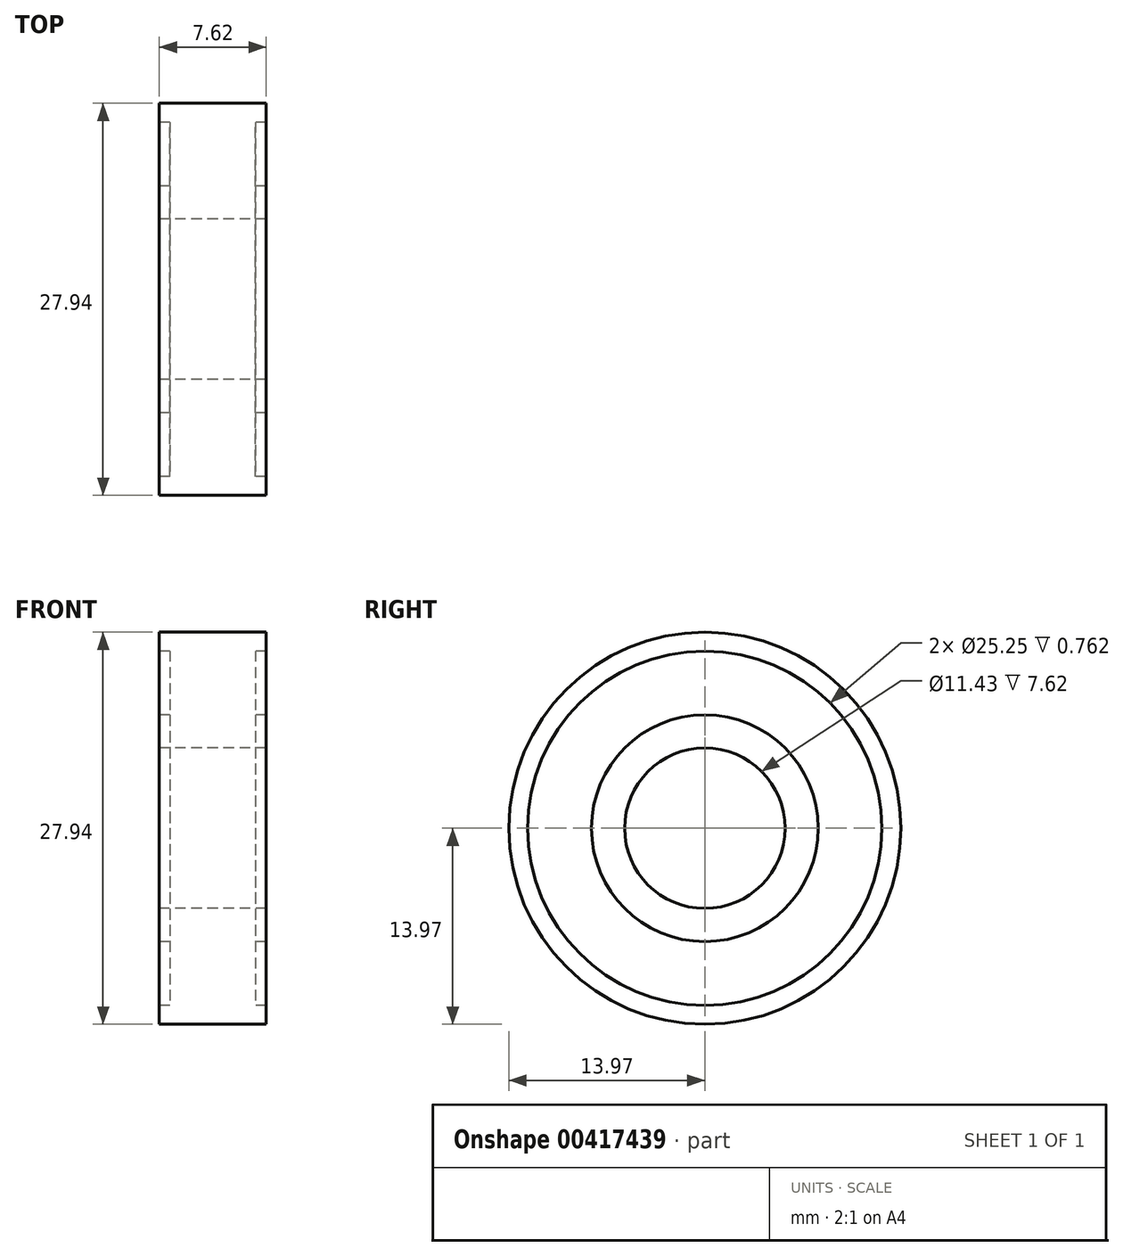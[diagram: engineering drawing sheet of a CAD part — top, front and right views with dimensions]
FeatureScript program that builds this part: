
annotation { "Feature Type Name" : "Feature", "Feature Type Description" : "" }
export const myFeature = defineFeature(function(context is Context, id is Id, definition is map)
    precondition{}
    {
        {
            var Q0;
            Q0=qCreatedBy(makeId("Top.planeOp"),FACE);
            var sketch = newSketch(context, id + "F0", { "sketchPlane" : qUnion([Q0])});
            skLineSegment(sketch, "E0", {"start": v(-3.8, -5.72) * mm, "end": v(3.81, -5.71) * mm});
            skLineSegment(sketch, "E1", {"start": v(3.81, -5.71) * mm, "end": v(3.81, -8.08) * mm});
            skLineSegment(sketch, "E2", {"start": v(3.81, -8.08) * mm, "end": v(3.05, -8.08) * mm});
            skLineSegment(sketch, "E3", {"start": v(3.05, -8.08) * mm, "end": v(3.05, -12.62) * mm});
            skLineSegment(sketch, "E4", {"start": v(3.05, -12.62) * mm, "end": v(3.81, -12.62) * mm});
            skLineSegment(sketch, "E5", {"start": v(3.81, -12.62) * mm, "end": v(3.81, -13.97) * mm});
            skLineSegment(sketch, "E6", {"start": v(3.81, -13.97) * mm, "end": v(-3.8, -13.97) * mm});
            skLineSegment(sketch, "E7", {"start": v(-12.1, 0) * mm, "end": v(9.84, 0) * mm});
            skLineSegment(sketch, "E8", {"start": v(-3.8, -5.72) * mm, "end": v(-3.8, -8.08) * mm});
            skLineSegment(sketch, "E9", {"start": v(-3.8, -8.08) * mm, "end": v(-3.05, -8.08) * mm});
            skLineSegment(sketch, "E10", {"start": v(-3.05, -8.08) * mm, "end": v(-3.05, -12.62) * mm});
            skLineSegment(sketch, "E11", {"start": v(-3.05, -12.62) * mm, "end": v(-3.8, -12.62) * mm});
            skLineSegment(sketch, "E12", {"start": v(-3.8, -12.62) * mm, "end": v(-3.8, -13.97) * mm});
            skSolve(sketch);
        }
        {
            var Q0;
            Q0=makeQuery(id+"F0.imprint","IMPRINT",FACE,{"disambiguationData":[TD([[makeQuery(id+"F0.imprint","IMPRINT",EDGE,{"derivedFrom":sQuery(id+"F0.wireOp",EDGE,"E0")}),-1.0]])]});
            var Q1;
            Q1=sQuery(id+"F0.wireOp",EDGE,"E7");
            revolve(context, id + "F1", {"entities" : qUnion([Q0]), "axis" : qUnion([Q1]), "revolveType" : RevolveType.FULL});
        }
    });
